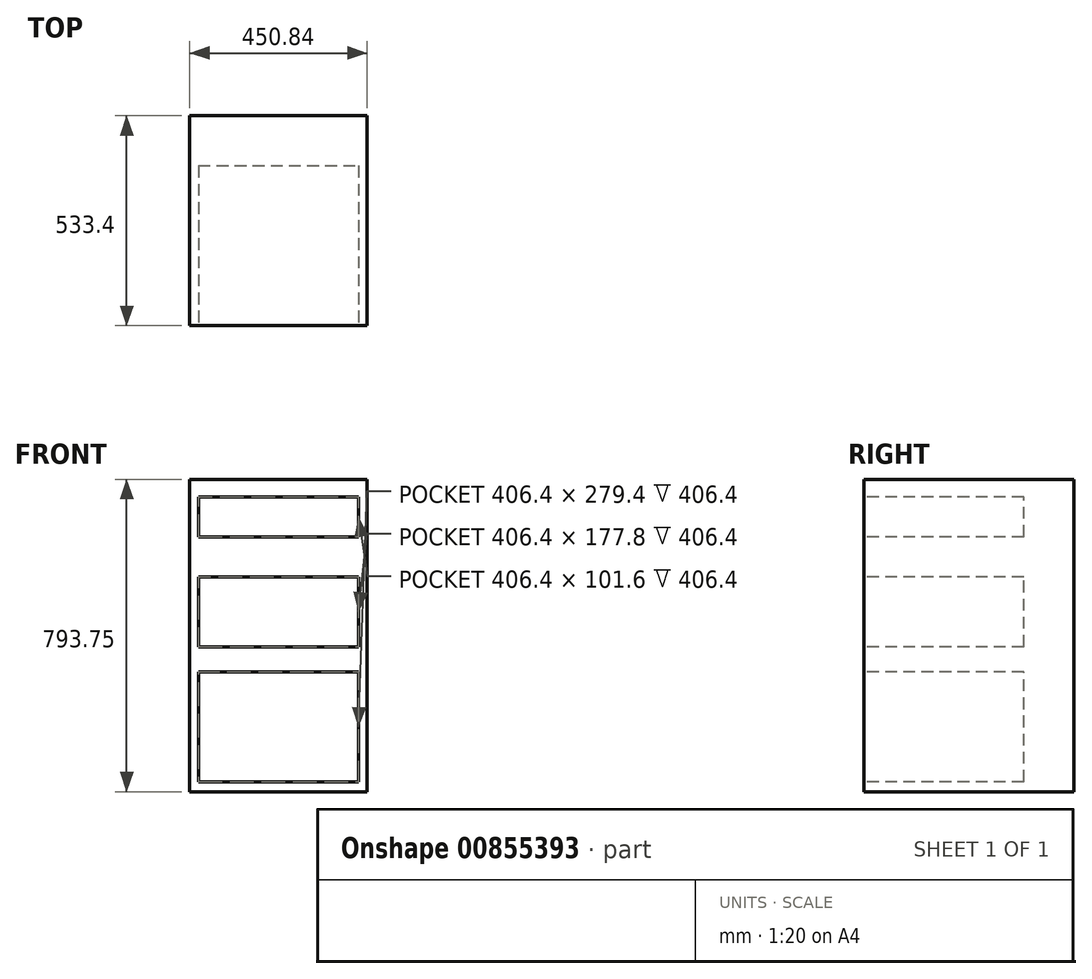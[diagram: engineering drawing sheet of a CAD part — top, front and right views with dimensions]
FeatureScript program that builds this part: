
annotation { "Feature Type Name" : "Feature", "Feature Type Description" : "" }
export const myFeature = defineFeature(function(context is Context, id is Id, definition is map)
    precondition{}
    {
        {
            var Q0;
            Q0=qCreatedBy(makeId("Top.planeOp"),FACE);
            var sketch = newSketch(context, id + "F0", { "sketchPlane" : qUnion([Q0])});
            skLineSegment(sketch, "E0.bottom", {"start": v(-225.42, -266.7) * mm, "end": v(225.43, -266.7) * mm});
            skLineSegment(sketch, "E0.top", {"start": v(-225.43, 266.7) * mm, "end": v(225.42, 266.7) * mm});
            skLineSegment(sketch, "E0.left", {"start": v(-225.42, -266.7) * mm, "end": v(-225.43, 266.7) * mm});
            skLineSegment(sketch, "E0.right", {"start": v(225.43, -266.7) * mm, "end": v(225.42, 266.7) * mm});
            skPoint(sketch, "E0.middle", {"position": v(0, 0) * mm});
            skSolve(sketch);
        }
        {
            var Q0;
            Q0=makeQuery(id+"F0.imprint","IMPRINT",FACE,{"disambiguationData":[TD([[makeQuery(id+"F0.imprint","IMPRINT",EDGE,{"derivedFrom":sQuery(id+"F0.wireOp",EDGE,"E0.bottom")}),1.0]])]});
            var Q1;
            Q1 = qSketchRegion(id + "F2", true);
            extrude(context, id + "F1", {"entities" : qUnion([Q0, Q1]), "oppositeDirection" : true, "depth" : 793.75 * mm, "offsetDistance" : 25 * mm});
        }
        {
            var Q0;
            Q0=makeQuery(id+"F1.opExtrude","SWEPT_FACE",FACE,{"disambiguationData":[OSD([sQuery(id+"F0.wireOp",EDGE,"E0.bottom")])]});
            var sketch = newSketch(context, id + "F2", { "sketchPlane" : qUnion([Q0])});
            skLineSegment(sketch, "E1.bottom", {"start": v(-203.2, -768.35) * mm, "end": v(203.2, -768.35) * mm});
            skLineSegment(sketch, "E1.top", {"start": v(-203.2, -488.95) * mm, "end": v(203.2, -488.95) * mm});
            skLineSegment(sketch, "E1.left", {"start": v(-203.2, -768.35) * mm, "end": v(-203.2, -488.95) * mm});
            skLineSegment(sketch, "E1.right", {"start": v(203.2, -768.35) * mm, "end": v(203.2, -488.95) * mm});
            skPoint(sketch, "E1.middle", {"position": v(0, -628.65) * mm});
            skLineSegment(sketch, "E2.bottom", {"start": v(-203.2, -425.45) * mm, "end": v(203.2, -425.45) * mm});
            skLineSegment(sketch, "E2.top", {"start": v(-203.2, -247.65) * mm, "end": v(203.2, -247.65) * mm});
            skLineSegment(sketch, "E2.left", {"start": v(-203.2, -425.45) * mm, "end": v(-203.2, -247.65) * mm});
            skLineSegment(sketch, "E2.right", {"start": v(203.2, -425.45) * mm, "end": v(203.2, -247.65) * mm});
            skPoint(sketch, "E2.middle", {"position": v(0, -336.55) * mm});
            skLineSegment(sketch, "E3.bottom", {"start": v(-203.2, -146.05) * mm, "end": v(203.2, -146.05) * mm});
            skLineSegment(sketch, "E3.top", {"start": v(-203.2, -44.45) * mm, "end": v(203.2, -44.45) * mm});
            skLineSegment(sketch, "E3.left", {"start": v(-203.2, -146.05) * mm, "end": v(-203.2, -44.45) * mm});
            skLineSegment(sketch, "E3.right", {"start": v(203.2, -146.05) * mm, "end": v(203.2, -44.45) * mm});
            skPoint(sketch, "E3.middle", {"position": v(0, -95.25) * mm});
            skSolve(sketch);
        }
        {
            var Q0;
            Q0=makeQuery(id+"F2.imprint","IMPRINT",FACE,{"disambiguationData":[TD([[makeQuery(id+"F2.imprint","IMPRINT",EDGE,{"derivedFrom":sQuery(id+"F2.wireOp",EDGE,"E3.bottom")}),1.0]])]});
            var Q1;
            Q1=makeQuery(id+"F2.imprint","IMPRINT",FACE,{"disambiguationData":[TD([[makeQuery(id+"F2.imprint","IMPRINT",EDGE,{"derivedFrom":sQuery(id+"F2.wireOp",EDGE,"E2.bottom")}),1.0]])]});
            var Q2;
            Q2=makeQuery(id+"F2.imprint","IMPRINT",FACE,{"disambiguationData":[TD([[makeQuery(id+"F2.imprint","IMPRINT",EDGE,{"derivedFrom":sQuery(id+"F2.wireOp",EDGE,"E1.bottom")}),1.0]])]});
            extrude(context, id + "F3", {"entities" : qUnion([Q0, Q1, Q2]), "operationType" : NewBodyOperationType.REMOVE, "oppositeDirection" : true, "depth" : 406.4 * mm, "offsetDistance" : 25 * mm});
        }
    });
